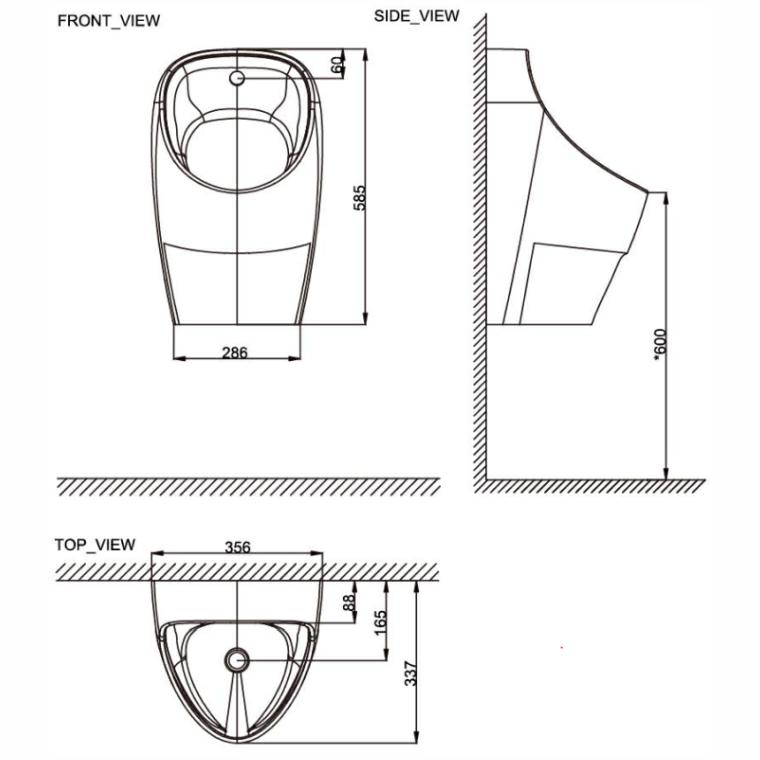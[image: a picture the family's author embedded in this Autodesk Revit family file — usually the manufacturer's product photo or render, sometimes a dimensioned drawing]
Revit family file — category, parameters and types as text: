
# Revit family: LIXIL - 705500WH - COBRA PAUSE URINAL
name_source: partatom
category: Plumbing Fixtures
units: mm (PartAtom-declared; Revit-internal decimal feet)

## family parameters
Always vertical = Yes
Cut with Voids When Loaded = No
Enable Cutting in Views = No
Maintain Annotation Orientation = No
OmniClass Number = 23.45.00.00
OmniClass Title = Sanitary, Laundry, and Cleaning Equipment
Part Type = Normal
Room Calculation Point = No
Round Connector Dimension = Use Diameter
Shared = Yes
Work Plane-Based = No

## types (1)
- 705500WH
    CW Connection Diameter = 55 mm
    CW Connection Radius = 28 mm
    Default Elevation = 0 mm  [stored 0 ft]
    Description = Cobra Pause urinal to detail and spec. See sanware schedule. Available from Lixil.
    Hosted on lixil.co.za = https://www.lixil.co.za
    M _ FLUSH UNIT = M _ LIXIL - STAINLESS STEEL 01
    M _ URINAL = M _ LIXIL - VAAL - PORCELAIN - WHITE 01
    Product Specification = Supplier: Lixil.
Product Description: Ultra Eco design to accommodate a water saving 0.9L flush. Compact concealed trapway. Suitable for commercial use. P-trap, hanging bracket set, back inlet braided hose and inlet connection elbows G1/2 included.
10 Year Warranty Cobra Genuine Cobra TeamAssist.
Product Code: CPSURWH1-6DT01.
SKU Code	: 705500WH.
Barcode: 6002194040262.
Brand: Cobra
Range: Pause.
Category: Plumbing Supplies.
Sub-Category: Urinals.
Material: Ceramic.
Colour: White.
Package Height: 370 mm
Package Width: 390 mm
Package Length: 610 mm
Package Volume: 88023000 mm³.
Package Weight: 21.72 kg

Notes:
- Refer to manufacturer's and supplier's installation, maintenance and cleaning manual.
- Refer to manufacturer's and supplier's guarantees and warrantees document.
    Waste Connection Diameter = 102 mm
    Waste Connection Radius = 51 mm

note: [stored X ft] marks values corroborated as IEEE doubles in the binary element streams (Revit-internal decimal feet)

## geometry (parser evidence)
native form markers: Sweep x10
no freeform markers — native parametric forms only
